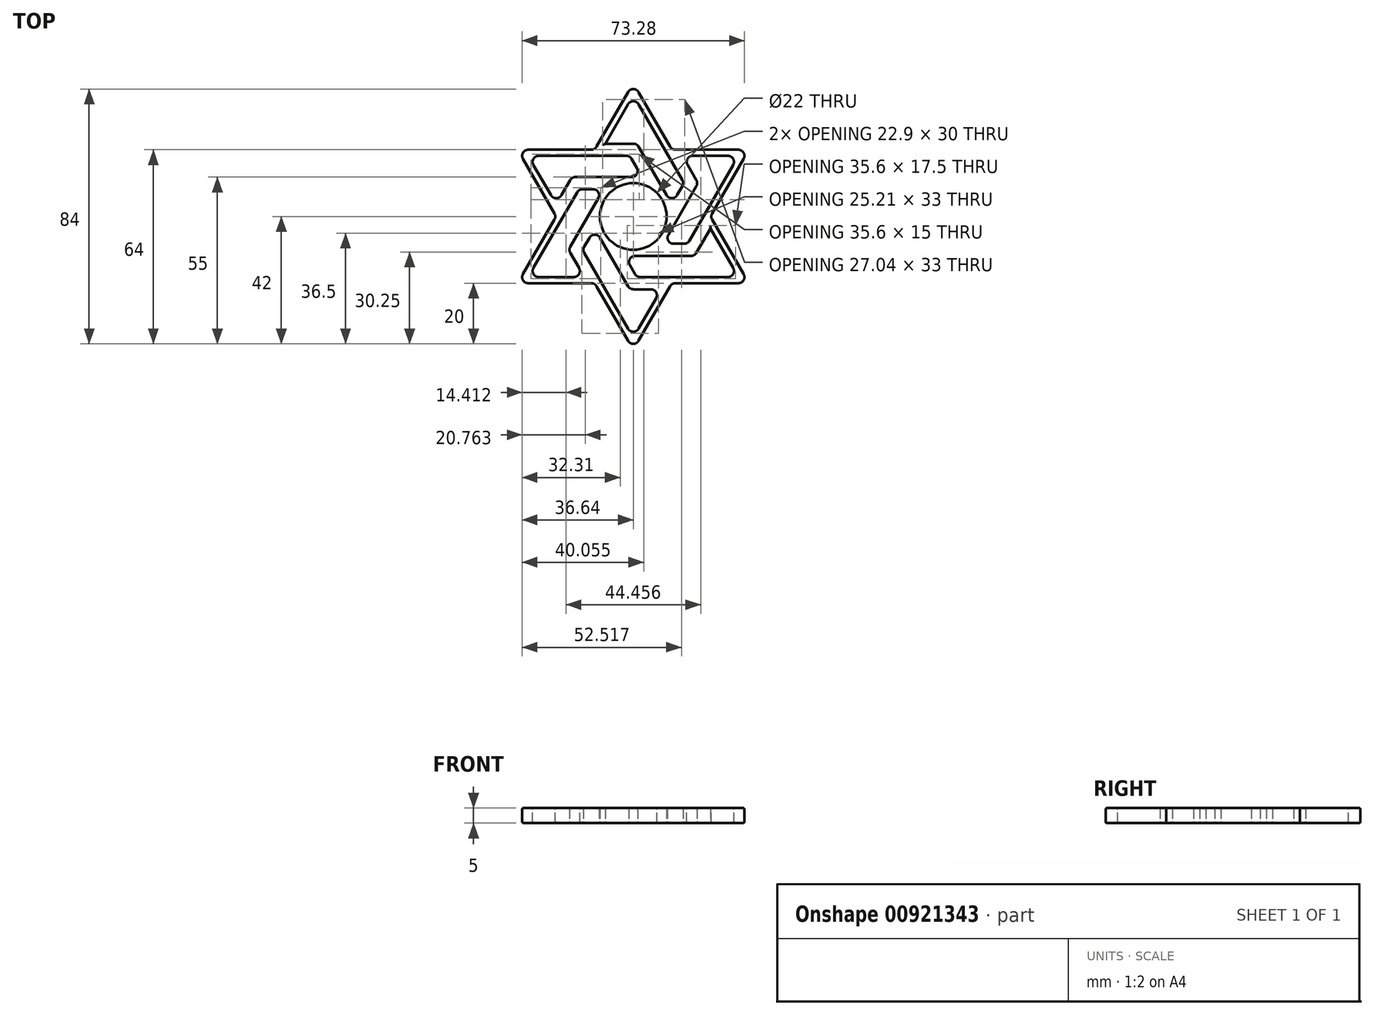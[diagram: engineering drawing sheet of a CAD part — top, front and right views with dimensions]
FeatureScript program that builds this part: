
annotation { "Feature Type Name" : "Feature", "Feature Type Description" : "" }
export const myFeature = defineFeature(function(context is Context, id is Id, definition is map)
    precondition{}
    {
        {
            var Q0;
            Q0=qCreatedBy(makeId("Top.planeOp"),FACE);
            var sketch = newSketch(context, id + "F0", { "sketchPlane" : qUnion([Q0])});
            skCircle(sketch, "E0", {"center": v(0, 0) * mm, "radius": 44 * mm});
            skCircle(sketch, "E1.cCircle", {"center": v(0, 0) * mm, "radius": 11 * mm});
            skLineSegment(sketch, "E1.0", {"start": v(0, 22) * mm, "end": v(12.7, 0) * mm, "construction": true});
            skLineSegment(sketch, "E1.1", {"start": v(19.05, 11) * mm, "end": v(6.35, -11) * mm, "construction": true});
            skLineSegment(sketch, "E1.2", {"start": v(19.05, -11) * mm, "end": v(-6.35, -11) * mm, "construction": true});
            skLineSegment(sketch, "E1.3", {"start": v(0, -22) * mm, "end": v(-12.7, 0) * mm, "construction": true});
            skLineSegment(sketch, "E1.4", {"start": v(-19.05, -11) * mm, "end": v(-6.35, 11) * mm, "construction": true});
            skLineSegment(sketch, "E1.5", {"start": v(-19.05, 11) * mm, "end": v(6.35, 11) * mm, "construction": true});
            skCircle(sketch, "E2", {"center": v(0, 0) * mm, "radius": 22 * mm, "construction": true});
            skLineSegment(sketch, "E3", {"start": v(0, 44) * mm, "end": v(38.1, -22) * mm, "construction": true});
            skLineSegment(sketch, "E4", {"start": v(38.1, -22) * mm, "end": v(-38.1, -22) * mm, "construction": true});
            skLineSegment(sketch, "E5", {"start": v(-38.1, -22) * mm, "end": v(0, 44) * mm, "construction": true});
            skLineSegment(sketch, "E6", {"start": v(0, -44) * mm, "end": v(38.1, 22) * mm, "construction": true});
            skLineSegment(sketch, "E7", {"start": v(38.1, 22) * mm, "end": v(-38.1, 22) * mm, "construction": true});
            skLineSegment(sketch, "E8", {"start": v(-38.1, 22) * mm, "end": v(0, -44) * mm, "construction": true});
            skLineSegment(sketch, "E9.0", {"start": v(34.64, 20) * mm, "end": v(16.17, 20) * mm});
            skLineSegment(sketch, "E9.1", {"start": v(17.9, -9) * mm, "end": v(34.64, 20) * mm});
            skLineSegment(sketch, "E10.0", {"start": v(16.17, 20) * mm, "end": v(21.36, 11) * mm});
            skLineSegment(sketch, "E11.0", {"start": v(21.36, 11) * mm, "end": v(9.81, -9) * mm});
            skLineSegment(sketch, "E12.0", {"start": v(17.9, -9) * mm, "end": v(9.81, -9) * mm});
            skLineSegment(sketch, "E13.1.0", {"start": v(16.74, 11) * mm, "end": v(0, 40) * mm});
            skLineSegment(sketch, "E13.1.1", {"start": v(16.74, 11) * mm, "end": v(12.7, 4) * mm});
            skLineSegment(sketch, "E13.1.2", {"start": v(1.15, 24) * mm, "end": v(12.7, 4) * mm});
            skLineSegment(sketch, "E13.1.3", {"start": v(-9.24, 24) * mm, "end": v(1.15, 24) * mm});
            skLineSegment(sketch, "E13.1.4", {"start": v(0, 40) * mm, "end": v(-9.24, 24) * mm});
            skLineSegment(sketch, "E13.2.0", {"start": v(-1.15, 20) * mm, "end": v(-34.64, 20) * mm});
            skLineSegment(sketch, "E13.2.1", {"start": v(-1.15, 20) * mm, "end": v(2.89, 13) * mm});
            skLineSegment(sketch, "E13.2.2", {"start": v(-20.2, 13) * mm, "end": v(2.89, 13) * mm});
            skLineSegment(sketch, "E13.2.3", {"start": v(-25.4, 4) * mm, "end": v(-20.2, 13) * mm});
            skLineSegment(sketch, "E13.2.4", {"start": v(-34.64, 20) * mm, "end": v(-25.4, 4) * mm});
            skLineSegment(sketch, "E13.3.0", {"start": v(-17.9, 9) * mm, "end": v(-34.64, -20) * mm});
            skLineSegment(sketch, "E13.3.1", {"start": v(-17.9, 9) * mm, "end": v(-9.81, 9) * mm});
            skLineSegment(sketch, "E13.3.2", {"start": v(-21.36, -11) * mm, "end": v(-9.81, 9) * mm});
            skLineSegment(sketch, "E13.3.3", {"start": v(-16.17, -20) * mm, "end": v(-21.36, -11) * mm});
            skLineSegment(sketch, "E13.3.4", {"start": v(-34.64, -20) * mm, "end": v(-16.17, -20) * mm});
            skLineSegment(sketch, "E13.4.0", {"start": v(-16.74, -11) * mm, "end": v(0, -40) * mm});
            skLineSegment(sketch, "E13.4.1", {"start": v(-16.74, -11) * mm, "end": v(-12.7, -4) * mm});
            skLineSegment(sketch, "E13.4.2", {"start": v(-1.15, -24) * mm, "end": v(-12.7, -4) * mm});
            skLineSegment(sketch, "E13.4.3", {"start": v(9.24, -24) * mm, "end": v(-1.15, -24) * mm});
            skLineSegment(sketch, "E13.4.4", {"start": v(0, -40) * mm, "end": v(9.24, -24) * mm});
            skLineSegment(sketch, "E13.5.0", {"start": v(1.15, -20) * mm, "end": v(34.64, -20) * mm});
            skLineSegment(sketch, "E13.5.1", {"start": v(1.15, -20) * mm, "end": v(-2.89, -13) * mm});
            skLineSegment(sketch, "E13.5.2", {"start": v(20.2, -13) * mm, "end": v(-2.89, -13) * mm});
            skLineSegment(sketch, "E13.5.3", {"start": v(25.4, -4) * mm, "end": v(20.2, -13) * mm});
            skLineSegment(sketch, "E13.5.4", {"start": v(34.64, -20) * mm, "end": v(25.4, -4) * mm});
            skSolve(sketch);
        }
        {
            var Q0;
            Q0 = qSketchRegion(id + "F0", true);
            extrude(context, id + "F1", {"entities" : qUnion([Q0]), "depth" : 2.5 * mm, "offsetDistance" : 25 * mm, "hasSecondDirection" : true, "secondDirectionOppositeDirection" : true, "secondDirectionDepth" : 2.5 * mm});
        }
        {
            var Q0;
            Q0=qCreatedBy(makeId("Top.planeOp"),FACE);
            var sketch = newSketch(context, id + "F2", { "sketchPlane" : qUnion([Q0])});
            skLineSegment(sketch, "E14", {"start": v(0, -44) * mm, "end": v(12.7, -22) * mm});
            skLineSegment(sketch, "E15", {"start": v(12.7, -22) * mm, "end": v(38.1, -22) * mm});
            skArc(sketch, "E16.0", {"start": v(0, -44) * mm, "mid": v(22, -38.1) * mm, "end": v(38.1, -22) * mm});
            skSolve(sketch);
        }
        {
            var Q0;
            Q0 = qSketchRegion(id + "F2", true);
            extrude(context, id + "F3", {"entities" : qUnion([Q0]), "depth" : 5 * mm, "offsetDistance" : 25 * mm, "hasSecondDirection" : true, "secondDirectionOppositeDirection" : true, "secondDirectionDepth" : 5 * mm});
        }
        {
            var Q0;
            Q0=makeQuery(id+"F3.opExtrude","SWEPT_BODY",BODY,{"disambiguationData":[OSD([sQuery(id+"F2.wireOp",EDGE,"E14"),sQuery(id+"F2.wireOp",EDGE,"E15"),sQuery(id+"F2.wireOp",EDGE,"E16.0")])]});
            var Q1;
            Q1=makeQuery(id+"F1.opExtrude","CAP_EDGE",EDGE,{"disambiguationData":[OSD([sQuery(id+"F0.wireOp",EDGE,"E1.cCircle")])],"isStart":false});
            circularPattern(context, id + "F4", {"operationType" : NewBodyOperationType.REMOVE, "entities" : qUnion([Q0]), "axis" : qUnion([Q1]), "angle" : 360 * degree, "instanceCount" : 6, "equalSpace" : true});
        }
        {
            var Q0;
            {var subQ0=sQuery(id+"F2.wireOp",EDGE,"E16.0");Q0=makeQuery(id+"F4.boolean.opBoolean","MERGE",EDGE,{"derivedFrom":[],"fromTools":[makeQuery(id+"F3.opExtrude","SWEPT_EDGE",EDGE,{"disambiguationData":[OSD([sQuery(id+"F2.wireOp",EDGE,"E15"),subQ0])]}),makeQuery(id+"F4.opPattern","COPY",EDGE,{"derivedFrom":makeQuery(id+"F3.opExtrude","SWEPT_EDGE",EDGE,{"disambiguationData":[OSD([sQuery(id+"F2.wireOp",EDGE,"E14"),subQ0])]}),"instanceName":"1"})]});}
            var Q1;
            {var subQ0=sQuery(id+"F2.wireOp",EDGE,"E16.0");Q1=makeQuery(id+"F4.boolean.opBoolean","MERGE",EDGE,{"derivedFrom":[],"fromTools":[makeQuery(id+"F4.opPattern","COPY",EDGE,{"derivedFrom":makeQuery(id+"F3.opExtrude","SWEPT_EDGE",EDGE,{"disambiguationData":[OSD([sQuery(id+"F2.wireOp",EDGE,"E15"),subQ0])]}),"instanceName":"1"}),makeQuery(id+"F4.opPattern","COPY",EDGE,{"derivedFrom":makeQuery(id+"F3.opExtrude","SWEPT_EDGE",EDGE,{"disambiguationData":[OSD([sQuery(id+"F2.wireOp",EDGE,"E14"),subQ0])]}),"instanceName":"2"})]});}
            var Q2;
            {var subQ0=sQuery(id+"F2.wireOp",EDGE,"E16.0");Q2=makeQuery(id+"F4.boolean.opBoolean","MERGE",EDGE,{"derivedFrom":[],"fromTools":[makeQuery(id+"F4.opPattern","COPY",EDGE,{"derivedFrom":makeQuery(id+"F3.opExtrude","SWEPT_EDGE",EDGE,{"disambiguationData":[OSD([sQuery(id+"F2.wireOp",EDGE,"E15"),subQ0])]}),"instanceName":"2"}),makeQuery(id+"F4.opPattern","COPY",EDGE,{"derivedFrom":makeQuery(id+"F3.opExtrude","SWEPT_EDGE",EDGE,{"disambiguationData":[OSD([sQuery(id+"F2.wireOp",EDGE,"E14"),subQ0])]}),"instanceName":"3"})]});}
            var Q3;
            Q3=makeQuery(id+"F1.opExtrude","SWEPT_EDGE",EDGE,{"disambiguationData":[OSD([sQuery(id+"F0.wireOp",EDGE,"E13.2.0"),sQuery(id+"F0.wireOp",EDGE,"E13.2.4")])]});
            var Q4;
            Q4=makeQuery(id+"F1.opExtrude","SWEPT_EDGE",EDGE,{"disambiguationData":[OSD([sQuery(id+"F0.wireOp",EDGE,"E13.3.0"),sQuery(id+"F0.wireOp",EDGE,"E13.3.1")])]});
            var Q5;
            Q5=makeQuery(id+"F1.opExtrude","SWEPT_EDGE",EDGE,{"disambiguationData":[OSD([sQuery(id+"F0.wireOp",EDGE,"E13.1.2"),sQuery(id+"F0.wireOp",EDGE,"E13.1.3")])]});
            var Q6;
            Q6=makeQuery(id+"F1.opExtrude","SWEPT_EDGE",EDGE,{"disambiguationData":[OSD([sQuery(id+"F0.wireOp",EDGE,"E9.0"),sQuery(id+"F0.wireOp",EDGE,"E10.0")])]});
            var Q7;
            Q7=makeQuery(id+"F1.opExtrude","SWEPT_EDGE",EDGE,{"disambiguationData":[OSD([sQuery(id+"F0.wireOp",EDGE,"E10.0"),sQuery(id+"F0.wireOp",EDGE,"E11.0")])]});
            var Q8;
            Q8=makeQuery(id+"F4.boolean.opBoolean","COPY",EDGE,{"derivedFrom":makeQuery(id+"F4.opPattern","COPY",EDGE,{"derivedFrom":makeQuery(id+"F3.opExtrude","SWEPT_EDGE",EDGE,{"disambiguationData":[OSD([sQuery(id+"F2.wireOp",EDGE,"E14"),sQuery(id+"F2.wireOp",EDGE,"E15")])]}),"instanceName":"1"})});
            var Q9;
            {var subQ0=sQuery(id+"F2.wireOp",EDGE,"E16.0");Q9=makeQuery(id+"F4.boolean.opBoolean","MERGE",EDGE,{"derivedFrom":[],"fromTools":[makeQuery(id+"F4.opPattern","COPY",EDGE,{"derivedFrom":makeQuery(id+"F3.opExtrude","SWEPT_EDGE",EDGE,{"disambiguationData":[OSD([sQuery(id+"F2.wireOp",EDGE,"E15"),subQ0])]}),"instanceName":"1"}),makeQuery(id+"F4.opPattern","COPY",EDGE,{"derivedFrom":makeQuery(id+"F3.opExtrude","SWEPT_EDGE",EDGE,{"disambiguationData":[OSD([sQuery(id+"F2.wireOp",EDGE,"E14"),subQ0])]}),"instanceName":"2"})]});}
            var Q10;
            Q10=makeQuery(id+"F1.opExtrude","SWEPT_EDGE",EDGE,{"disambiguationData":[OSD([sQuery(id+"F0.wireOp",EDGE,"E13.5.2"),sQuery(id+"F0.wireOp",EDGE,"E13.5.3")])]});
            var Q11;
            {var subQ0=sQuery(id+"F2.wireOp",EDGE,"E16.0");Q11=makeQuery(id+"F4.boolean.opBoolean","MERGE",EDGE,{"derivedFrom":[],"fromTools":[makeQuery(id+"F3.opExtrude","SWEPT_EDGE",EDGE,{"disambiguationData":[OSD([sQuery(id+"F2.wireOp",EDGE,"E15"),subQ0])]}),makeQuery(id+"F4.opPattern","COPY",EDGE,{"derivedFrom":makeQuery(id+"F3.opExtrude","SWEPT_EDGE",EDGE,{"disambiguationData":[OSD([sQuery(id+"F2.wireOp",EDGE,"E14"),subQ0])]}),"instanceName":"1"})]});}
            var Q12;
            Q12=makeQuery(id+"F4.boolean.opBoolean","COPY",EDGE,{"derivedFrom":makeQuery(id+"F3.opExtrude","SWEPT_EDGE",EDGE,{"disambiguationData":[OSD([sQuery(id+"F2.wireOp",EDGE,"E14"),sQuery(id+"F2.wireOp",EDGE,"E15")])]})});
            var Q13;
            {var subQ0=sQuery(id+"F2.wireOp",EDGE,"E16.0");Q13=makeQuery(id+"F4.boolean.opBoolean","MERGE",EDGE,{"derivedFrom":[],"fromTools":[makeQuery(id+"F3.opExtrude","SWEPT_EDGE",EDGE,{"disambiguationData":[OSD([sQuery(id+"F2.wireOp",EDGE,"E14"),subQ0])]}),makeQuery(id+"F4.opPattern","COPY",EDGE,{"derivedFrom":makeQuery(id+"F3.opExtrude","SWEPT_EDGE",EDGE,{"disambiguationData":[OSD([sQuery(id+"F2.wireOp",EDGE,"E15"),subQ0])]}),"instanceName":"5"})]});}
            var Q14;
            {var subQ0=sQuery(id+"F2.wireOp",EDGE,"E16.0");Q14=makeQuery(id+"F4.boolean.opBoolean","MERGE",EDGE,{"derivedFrom":[],"fromTools":[makeQuery(id+"F4.opPattern","COPY",EDGE,{"derivedFrom":makeQuery(id+"F3.opExtrude","SWEPT_EDGE",EDGE,{"disambiguationData":[OSD([sQuery(id+"F2.wireOp",EDGE,"E15"),subQ0])]}),"instanceName":"4"}),makeQuery(id+"F4.opPattern","COPY",EDGE,{"derivedFrom":makeQuery(id+"F3.opExtrude","SWEPT_EDGE",EDGE,{"disambiguationData":[OSD([sQuery(id+"F2.wireOp",EDGE,"E14"),subQ0])]}),"instanceName":"5"})]});}
            var Q15;
            Q15=makeQuery(id+"F1.opExtrude","SWEPT_EDGE",EDGE,{"disambiguationData":[OSD([sQuery(id+"F0.wireOp",EDGE,"E13.4.0"),sQuery(id+"F0.wireOp",EDGE,"E13.4.1")])]});
            var Q16;
            Q16=makeQuery(id+"F1.opExtrude","SWEPT_EDGE",EDGE,{"disambiguationData":[OSD([sQuery(id+"F0.wireOp",EDGE,"E13.5.1"),sQuery(id+"F0.wireOp",EDGE,"E13.5.2")])]});
            var Q17;
            Q17=makeQuery(id+"F1.opExtrude","SWEPT_EDGE",EDGE,{"disambiguationData":[OSD([sQuery(id+"F0.wireOp",EDGE,"E13.4.2"),sQuery(id+"F0.wireOp",EDGE,"E13.4.3")])]});
            var Q18;
            {var subQ0=sQuery(id+"F2.wireOp",EDGE,"E16.0");Q18=makeQuery(id+"F4.boolean.opBoolean","MERGE",EDGE,{"derivedFrom":[],"fromTools":[makeQuery(id+"F3.opExtrude","SWEPT_EDGE",EDGE,{"disambiguationData":[OSD([sQuery(id+"F2.wireOp",EDGE,"E14"),subQ0])]}),makeQuery(id+"F4.opPattern","COPY",EDGE,{"derivedFrom":makeQuery(id+"F3.opExtrude","SWEPT_EDGE",EDGE,{"disambiguationData":[OSD([sQuery(id+"F2.wireOp",EDGE,"E15"),subQ0])]}),"instanceName":"5"})]});}
            var Q19;
            Q19=makeQuery(id+"F1.opExtrude","SWEPT_EDGE",EDGE,{"disambiguationData":[OSD([sQuery(id+"F0.wireOp",EDGE,"E11.0"),sQuery(id+"F0.wireOp",EDGE,"E12.0")])]});
            var Q20;
            Q20=makeQuery(id+"F1.opExtrude","SWEPT_EDGE",EDGE,{"disambiguationData":[OSD([sQuery(id+"F0.wireOp",EDGE,"E13.3.0"),sQuery(id+"F0.wireOp",EDGE,"E13.3.4")])]});
            var Q21;
            Q21=makeQuery(id+"F1.opExtrude","SWEPT_EDGE",EDGE,{"disambiguationData":[OSD([sQuery(id+"F0.wireOp",EDGE,"E13.4.0"),sQuery(id+"F0.wireOp",EDGE,"E13.4.4")])]});
            var Q22;
            Q22=makeQuery(id+"F1.opExtrude","SWEPT_EDGE",EDGE,{"disambiguationData":[OSD([sQuery(id+"F0.wireOp",EDGE,"E13.2.3"),sQuery(id+"F0.wireOp",EDGE,"E13.2.4")])]});
            var Q23;
            Q23=makeQuery(id+"F1.opExtrude","SWEPT_EDGE",EDGE,{"disambiguationData":[OSD([sQuery(id+"F0.wireOp",EDGE,"E13.2.2"),sQuery(id+"F0.wireOp",EDGE,"E13.2.3")])]});
            var Q24;
            Q24=makeQuery(id+"F1.opExtrude","SWEPT_EDGE",EDGE,{"disambiguationData":[OSD([sQuery(id+"F0.wireOp",EDGE,"E13.1.1"),sQuery(id+"F0.wireOp",EDGE,"E13.1.2")])]});
            var Q25;
            Q25=makeQuery(id+"F1.opExtrude","SWEPT_EDGE",EDGE,{"disambiguationData":[OSD([sQuery(id+"F0.wireOp",EDGE,"E13.4.3"),sQuery(id+"F0.wireOp",EDGE,"E13.4.4")])]});
            var Q26;
            Q26=makeQuery(id+"F1.opExtrude","SWEPT_EDGE",EDGE,{"disambiguationData":[OSD([sQuery(id+"F0.wireOp",EDGE,"E13.1.0"),sQuery(id+"F0.wireOp",EDGE,"E13.1.1")])]});
            var Q27;
            Q27=makeQuery(id+"F1.opExtrude","SWEPT_EDGE",EDGE,{"disambiguationData":[OSD([sQuery(id+"F0.wireOp",EDGE,"E9.0"),sQuery(id+"F0.wireOp",EDGE,"E9.1")])]});
            var Q28;
            Q28=makeQuery(id+"F1.opExtrude","SWEPT_EDGE",EDGE,{"disambiguationData":[OSD([sQuery(id+"F0.wireOp",EDGE,"E13.2.0"),sQuery(id+"F0.wireOp",EDGE,"E13.2.1")])]});
            var Q29;
            Q29=makeQuery(id+"F1.opExtrude","SWEPT_EDGE",EDGE,{"disambiguationData":[OSD([sQuery(id+"F0.wireOp",EDGE,"E13.3.1"),sQuery(id+"F0.wireOp",EDGE,"E13.3.2")])]});
            var Q30;
            Q30=makeQuery(id+"F1.opExtrude","SWEPT_EDGE",EDGE,{"disambiguationData":[OSD([sQuery(id+"F0.wireOp",EDGE,"E13.3.2"),sQuery(id+"F0.wireOp",EDGE,"E13.3.3")])]});
            var Q31;
            Q31=makeQuery(id+"F1.opExtrude","SWEPT_EDGE",EDGE,{"disambiguationData":[OSD([sQuery(id+"F0.wireOp",EDGE,"E13.5.0"),sQuery(id+"F0.wireOp",EDGE,"E13.5.1")])]});
            var Q32;
            Q32=makeQuery(id+"F1.opExtrude","SWEPT_EDGE",EDGE,{"disambiguationData":[OSD([sQuery(id+"F0.wireOp",EDGE,"E13.5.0"),sQuery(id+"F0.wireOp",EDGE,"E13.5.4")])]});
            var Q33;
            Q33=makeQuery(id+"F1.opExtrude","SWEPT_EDGE",EDGE,{"disambiguationData":[OSD([sQuery(id+"F0.wireOp",EDGE,"E13.2.1"),sQuery(id+"F0.wireOp",EDGE,"E13.2.2")])]});
            var Q34;
            Q34=makeQuery(id+"F4.boolean.opBoolean","COPY",EDGE,{"derivedFrom":makeQuery(id+"F4.opPattern","COPY",EDGE,{"derivedFrom":makeQuery(id+"F3.opExtrude","SWEPT_EDGE",EDGE,{"disambiguationData":[OSD([sQuery(id+"F2.wireOp",EDGE,"E14"),sQuery(id+"F2.wireOp",EDGE,"E15")])]}),"instanceName":"4"})});
            var Q35;
            Q35=makeQuery(id+"F4.boolean.opBoolean","COPY",EDGE,{"derivedFrom":makeQuery(id+"F4.opPattern","COPY",EDGE,{"derivedFrom":makeQuery(id+"F3.opExtrude","SWEPT_EDGE",EDGE,{"disambiguationData":[OSD([sQuery(id+"F2.wireOp",EDGE,"E14"),sQuery(id+"F2.wireOp",EDGE,"E15")])]}),"instanceName":"3"})});
            var Q36;
            {var subQ0=sQuery(id+"F2.wireOp",EDGE,"E16.0");Q36=makeQuery(id+"F4.boolean.opBoolean","MERGE",EDGE,{"derivedFrom":[],"fromTools":[makeQuery(id+"F4.opPattern","COPY",EDGE,{"derivedFrom":makeQuery(id+"F3.opExtrude","SWEPT_EDGE",EDGE,{"disambiguationData":[OSD([sQuery(id+"F2.wireOp",EDGE,"E15"),subQ0])]}),"instanceName":"2"}),makeQuery(id+"F4.opPattern","COPY",EDGE,{"derivedFrom":makeQuery(id+"F3.opExtrude","SWEPT_EDGE",EDGE,{"disambiguationData":[OSD([sQuery(id+"F2.wireOp",EDGE,"E14"),subQ0])]}),"instanceName":"3"})]});}
            var Q37;
            Q37=makeQuery(id+"F1.opExtrude","SWEPT_EDGE",EDGE,{"disambiguationData":[OSD([sQuery(id+"F0.wireOp",EDGE,"E13.1.0"),sQuery(id+"F0.wireOp",EDGE,"E13.1.4")])]});
            var Q38;
            Q38=makeQuery(id+"F1.opExtrude","SWEPT_EDGE",EDGE,{"disambiguationData":[OSD([sQuery(id+"F0.wireOp",EDGE,"E13.4.1"),sQuery(id+"F0.wireOp",EDGE,"E13.4.2")])]});
            var Q39;
            Q39=makeQuery(id+"F4.boolean.opBoolean","COPY",EDGE,{"derivedFrom":makeQuery(id+"F4.opPattern","COPY",EDGE,{"derivedFrom":makeQuery(id+"F3.opExtrude","SWEPT_EDGE",EDGE,{"disambiguationData":[OSD([sQuery(id+"F2.wireOp",EDGE,"E14"),sQuery(id+"F2.wireOp",EDGE,"E15")])]}),"instanceName":"5"})});
            var Q40;
            Q40=makeQuery(id+"F1.opExtrude","SWEPT_EDGE",EDGE,{"disambiguationData":[OSD([sQuery(id+"F0.wireOp",EDGE,"E13.3.3"),sQuery(id+"F0.wireOp",EDGE,"E13.3.4")])]});
            var Q41;
            Q41=makeQuery(id+"F4.boolean.opBoolean","COPY",EDGE,{"derivedFrom":makeQuery(id+"F4.opPattern","COPY",EDGE,{"derivedFrom":makeQuery(id+"F3.opExtrude","SWEPT_EDGE",EDGE,{"disambiguationData":[OSD([sQuery(id+"F2.wireOp",EDGE,"E14"),sQuery(id+"F2.wireOp",EDGE,"E15")])]}),"instanceName":"2"})});
            var Q42;
            Q42=makeQuery(id+"F1.opExtrude","SWEPT_EDGE",EDGE,{"disambiguationData":[OSD([sQuery(id+"F0.wireOp",EDGE,"E9.1"),sQuery(id+"F0.wireOp",EDGE,"E12.0")])]});
            var Q43;
            {var subQ0=sQuery(id+"F2.wireOp",EDGE,"E16.0");Q43=makeQuery(id+"F4.boolean.opBoolean","MERGE",EDGE,{"derivedFrom":[],"fromTools":[makeQuery(id+"F4.opPattern","COPY",EDGE,{"derivedFrom":makeQuery(id+"F3.opExtrude","SWEPT_EDGE",EDGE,{"disambiguationData":[OSD([sQuery(id+"F2.wireOp",EDGE,"E15"),subQ0])]}),"instanceName":"3"}),makeQuery(id+"F4.opPattern","COPY",EDGE,{"derivedFrom":makeQuery(id+"F3.opExtrude","SWEPT_EDGE",EDGE,{"disambiguationData":[OSD([sQuery(id+"F2.wireOp",EDGE,"E14"),subQ0])]}),"instanceName":"4"})]});}
            fillet(context, id + "F5", {"entities" : qUnion([Q0, Q1, Q2, Q3, Q4, Q5, Q6, Q7, Q8, Q9, Q10, Q11, Q12, Q13, Q14, Q15, Q16, Q17, Q18, Q19, Q20, Q21, Q22, Q23, Q24, Q25, Q26, Q27, Q28, Q29, Q30, Q31, Q32, Q33, Q34, Q35, Q36, Q37, Q38, Q39, Q40, Q41, Q42, Q43]), "radius" : 2 * mm, "tangentPropagation" : true, "allowEdgeOverflow" : false});
        }
        {
            var Q0;
            Q0=qCreatedBy(makeId("Top.planeOp"),FACE);
            var sketch = newSketch(context, id + "F6", { "sketchPlane" : qUnion([Q0])});
            skArc(sketch, "E17", {"start": v(-1.73, -41) * mm, "mid": v(0, -42) * mm, "end": v(1.73, -41) * mm});
            skLineSegment(sketch, "E18.0", {"start": v(0, -44) * mm, "end": v(-1.73, -41) * mm});
            skLineSegment(sketch, "E19.0", {"start": v(1.73, -41) * mm, "end": v(0, -44) * mm});
            skPoint(sketch, "E20.orphan", {"position": v(-12.12, -23) * mm});
            skPoint(sketch, "E21.orphan", {"position": v(12.12, -23) * mm});
            skSolve(sketch);
        }
        {
            var Q0;
            Q0 = qSketchRegion(id + "F6", true);
            extrude(context, id + "F7", {"entities" : qUnion([Q0]), "depth" : 5 * mm, "offsetDistance" : 25 * mm, "hasSecondDirection" : true, "secondDirectionOppositeDirection" : true, "secondDirectionDepth" : 5 * mm});
        }
        {
            var Q0;
            Q0=makeQuery(id+"F7.opExtrude","SWEPT_BODY",BODY,{"disambiguationData":[OSD([sQuery(id+"F6.wireOp",EDGE,"E17"),sQuery(id+"F6.wireOp",EDGE,"E18.0"),sQuery(id+"F6.wireOp",EDGE,"E19.0")])]});
            var Q1;
            Q1=makeQuery(id+"F1.opExtrude","CAP_EDGE",EDGE,{"disambiguationData":[OSD([sQuery(id+"F0.wireOp",EDGE,"E1.cCircle")])],"isStart":false});
            circularPattern(context, id + "F8", {"operationType" : NewBodyOperationType.REMOVE, "entities" : qUnion([Q0]), "axis" : qUnion([Q1]), "angle" : 360 * degree, "instanceCount" : 6, "equalSpace" : true});
        }
        {
            var Q0;
            Q0=makeQuery(id+"F1.opExtrude","CAP_FACE",FACE,{"disambiguationData":[OSD([sQuery(id+"F0.wireOp",EDGE,"E0"),sQuery(id+"F0.wireOp",EDGE,"E1.cCircle"),sQuery(id+"F0.wireOp",EDGE,"E9.0"),sQuery(id+"F0.wireOp",EDGE,"E9.1"),sQuery(id+"F0.wireOp",EDGE,"E10.0"),sQuery(id+"F0.wireOp",EDGE,"E11.0"),sQuery(id+"F0.wireOp",EDGE,"E12.0"),sQuery(id+"F0.wireOp",EDGE,"E13.1.0"),sQuery(id+"F0.wireOp",EDGE,"E13.1.1"),sQuery(id+"F0.wireOp",EDGE,"E13.1.2"),sQuery(id+"F0.wireOp",EDGE,"E13.1.3"),sQuery(id+"F0.wireOp",EDGE,"E13.1.4"),sQuery(id+"F0.wireOp",EDGE,"E13.2.0"),sQuery(id+"F0.wireOp",EDGE,"E13.2.1"),sQuery(id+"F0.wireOp",EDGE,"E13.2.2"),sQuery(id+"F0.wireOp",EDGE,"E13.2.3"),sQuery(id+"F0.wireOp",EDGE,"E13.2.4"),sQuery(id+"F0.wireOp",EDGE,"E13.3.0"),sQuery(id+"F0.wireOp",EDGE,"E13.3.1"),sQuery(id+"F0.wireOp",EDGE,"E13.3.2"),sQuery(id+"F0.wireOp",EDGE,"E13.3.3"),sQuery(id+"F0.wireOp",EDGE,"E13.3.4"),sQuery(id+"F0.wireOp",EDGE,"E13.4.0"),sQuery(id+"F0.wireOp",EDGE,"E13.4.1"),sQuery(id+"F0.wireOp",EDGE,"E13.4.2"),sQuery(id+"F0.wireOp",EDGE,"E13.4.3"),sQuery(id+"F0.wireOp",EDGE,"E13.4.4"),sQuery(id+"F0.wireOp",EDGE,"E13.5.0"),sQuery(id+"F0.wireOp",EDGE,"E13.5.1"),sQuery(id+"F0.wireOp",EDGE,"E13.5.2"),sQuery(id+"F0.wireOp",EDGE,"E13.5.3"),sQuery(id+"F0.wireOp",EDGE,"E13.5.4")])],"isStart":false});
            var Q1;
            Q1=makeQuery(id+"F1.opExtrude","CAP_FACE",FACE,{"disambiguationData":[OSD([sQuery(id+"F0.wireOp",EDGE,"E0"),sQuery(id+"F0.wireOp",EDGE,"E1.cCircle"),sQuery(id+"F0.wireOp",EDGE,"E9.0"),sQuery(id+"F0.wireOp",EDGE,"E9.1"),sQuery(id+"F0.wireOp",EDGE,"E10.0"),sQuery(id+"F0.wireOp",EDGE,"E11.0"),sQuery(id+"F0.wireOp",EDGE,"E12.0"),sQuery(id+"F0.wireOp",EDGE,"E13.1.0"),sQuery(id+"F0.wireOp",EDGE,"E13.1.1"),sQuery(id+"F0.wireOp",EDGE,"E13.1.2"),sQuery(id+"F0.wireOp",EDGE,"E13.1.3"),sQuery(id+"F0.wireOp",EDGE,"E13.1.4"),sQuery(id+"F0.wireOp",EDGE,"E13.2.0"),sQuery(id+"F0.wireOp",EDGE,"E13.2.1"),sQuery(id+"F0.wireOp",EDGE,"E13.2.2"),sQuery(id+"F0.wireOp",EDGE,"E13.2.3"),sQuery(id+"F0.wireOp",EDGE,"E13.2.4"),sQuery(id+"F0.wireOp",EDGE,"E13.3.0"),sQuery(id+"F0.wireOp",EDGE,"E13.3.1"),sQuery(id+"F0.wireOp",EDGE,"E13.3.2"),sQuery(id+"F0.wireOp",EDGE,"E13.3.3"),sQuery(id+"F0.wireOp",EDGE,"E13.3.4"),sQuery(id+"F0.wireOp",EDGE,"E13.4.0"),sQuery(id+"F0.wireOp",EDGE,"E13.4.1"),sQuery(id+"F0.wireOp",EDGE,"E13.4.2"),sQuery(id+"F0.wireOp",EDGE,"E13.4.3"),sQuery(id+"F0.wireOp",EDGE,"E13.4.4"),sQuery(id+"F0.wireOp",EDGE,"E13.5.0"),sQuery(id+"F0.wireOp",EDGE,"E13.5.1"),sQuery(id+"F0.wireOp",EDGE,"E13.5.2"),sQuery(id+"F0.wireOp",EDGE,"E13.5.3"),sQuery(id+"F0.wireOp",EDGE,"E13.5.4")])],"isStart":true});
            fillet(context, id + "F9", {"entities" : qUnion([Q0, Q1]), "radius" : 0.5 * mm, "tangentPropagation" : true, "allowEdgeOverflow" : false});
        }
    });
